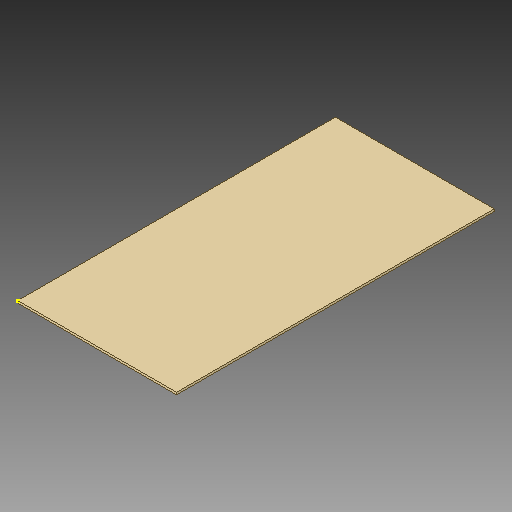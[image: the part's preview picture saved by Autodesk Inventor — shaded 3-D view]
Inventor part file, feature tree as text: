
AUTODESK INVENTOR PART (.ipt)
format: ipt  version: 2018 (Build 220112000, 112)  size: 102,912 bytes
history: native  units: in
note: dims shown in document units (in); Inventor stores cm internally (conversion verified against a paired STEP export)
features: sketch x2, extrude x1
ambient origin geometry x8: Origin, YZ Plane, XZ Plane, XY Plane, X Axis, Y Axis, Z Axis, Center Point
bodies: Solid1 (feature_tree)
feature tree (3):
  extrude  "Extrusion1"  Depth=1440.0in
  sketch  "Sketch2"  dims[d2=10.0in d3=0.0in]
  sketch  "Sketch1"  dims[d0=720.0in d1=1440.0in]
